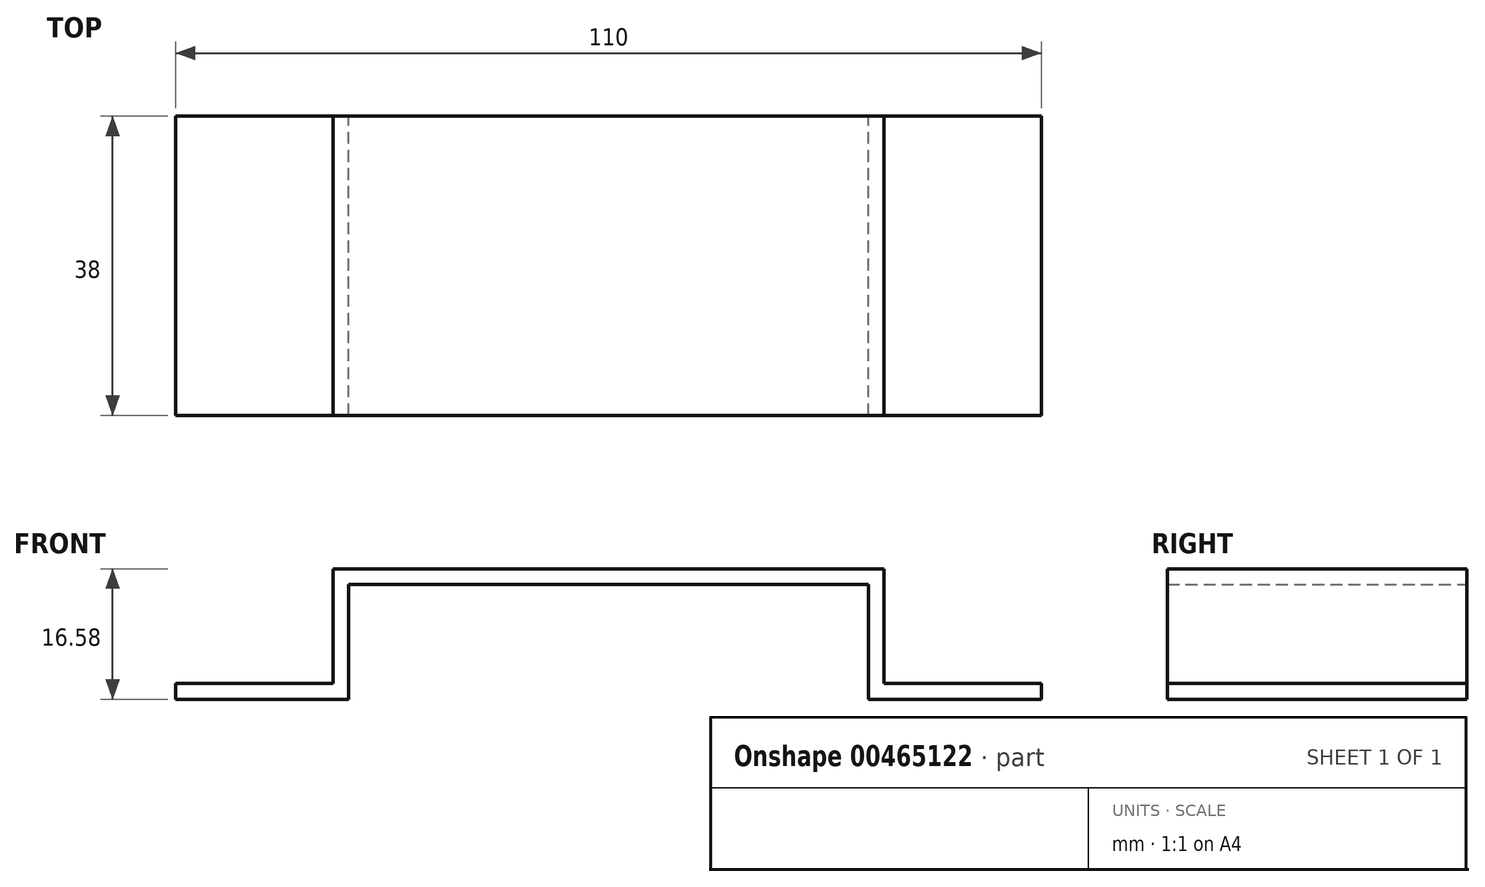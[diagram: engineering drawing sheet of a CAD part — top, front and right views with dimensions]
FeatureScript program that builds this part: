
annotation { "Feature Type Name" : "Feature", "Feature Type Description" : "" }
export const myFeature = defineFeature(function(context is Context, id is Id, definition is map)
    precondition{}
    {
        {
            var Q0;
            Q0=qCreatedBy(makeId("Front.planeOp"),FACE);
            var sketch = newSketch(context, id + "F0", { "sketchPlane" : qUnion([Q0])});
            skLineSegment(sketch, "E0", {"start": v(-65.47, 0) * mm, "end": v(-45.47, 0) * mm});
            skLineSegment(sketch, "E1", {"start": v(-45.47, 0) * mm, "end": v(-45.47, 14.58) * mm});
            skLineSegment(sketch, "E2", {"start": v(24.53, 14.58) * mm, "end": v(-45.47, 14.58) * mm});
            skLineSegment(sketch, "E3", {"start": v(24.53, 14.58) * mm, "end": v(24.53, 0) * mm});
            skLineSegment(sketch, "E4", {"start": v(24.53, 0) * mm, "end": v(44.53, 0) * mm});
            skLineSegment(sketch, "E5.0", {"start": v(-65.47, -2) * mm, "end": v(-45.47, -2) * mm});
            skLineSegment(sketch, "E6.0", {"start": v(-43.47, 0) * mm, "end": v(-43.47, 12.58) * mm});
            skLineSegment(sketch, "E7.0", {"start": v(22.53, 12.58) * mm, "end": v(-43.47, 12.58) * mm});
            skLineSegment(sketch, "E8.0", {"start": v(22.53, 12.58) * mm, "end": v(22.53, 0) * mm});
            skLineSegment(sketch, "E9.0", {"start": v(24.53, -2) * mm, "end": v(44.53, -2) * mm});
            skLineSegment(sketch, "E10", {"start": v(-43.47, 0) * mm, "end": v(-43.47, -2) * mm});
            skLineSegment(sketch, "E11", {"start": v(-45.47, -2) * mm, "end": v(-43.47, -2) * mm});
            skLineSegment(sketch, "E12", {"start": v(-65.47, -2) * mm, "end": v(-65.47, 0) * mm});
            skLineSegment(sketch, "E13", {"start": v(22.53, 0) * mm, "end": v(22.53, -2) * mm});
            skLineSegment(sketch, "E14", {"start": v(22.53, -2) * mm, "end": v(24.53, -2) * mm});
            skLineSegment(sketch, "E15", {"start": v(44.53, -2) * mm, "end": v(44.53, 0) * mm});
            skSolve(sketch);
        }
        {
            var Q0;
            Q0=makeQuery(id+"F0.imprint","IMPRINT",FACE,{"disambiguationData":[TD([[makeQuery(id+"F0.imprint","IMPRINT",EDGE,{"derivedFrom":sQuery(id+"F0.wireOp",EDGE,"E0")}),-1.0]])]});
            extrude(context, id + "F1", {"entities" : qUnion([Q0]), "depth" : 38 * mm});
        }
    });
